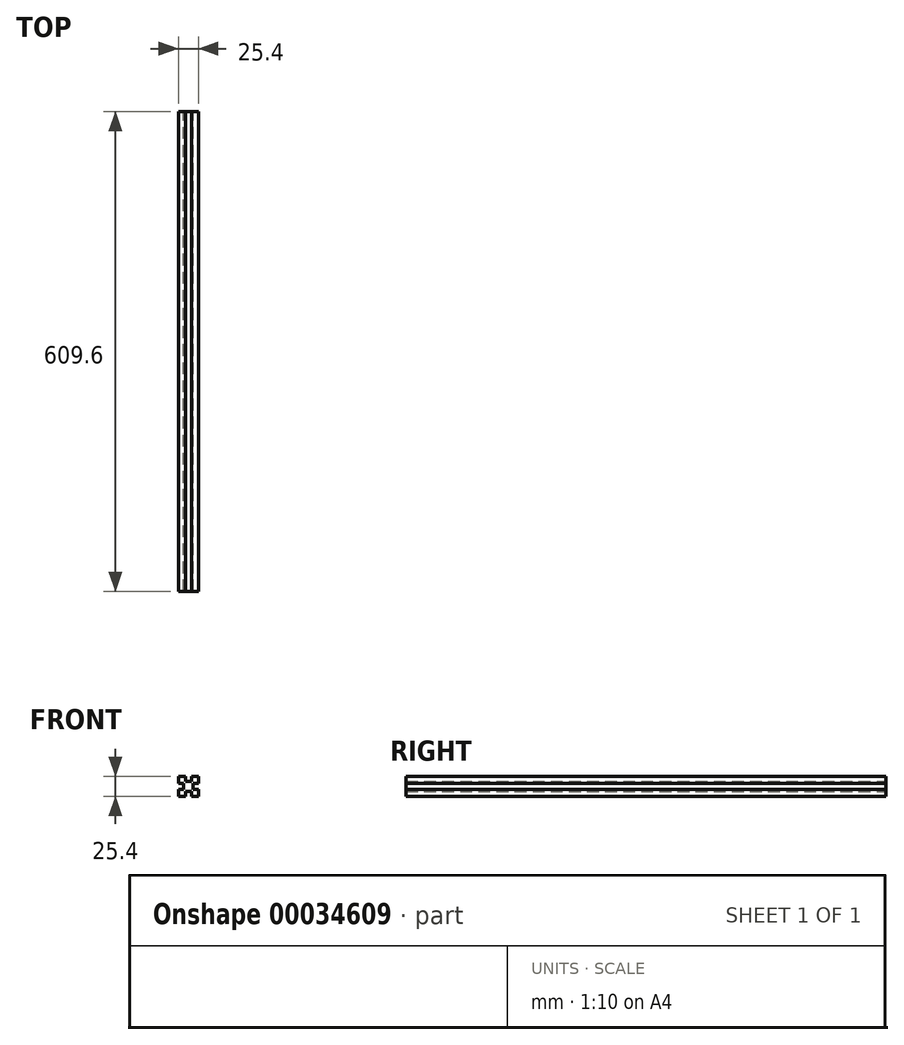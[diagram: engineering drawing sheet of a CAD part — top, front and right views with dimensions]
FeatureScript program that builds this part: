
annotation { "Feature Type Name" : "Feature", "Feature Type Description" : "" }
export const myFeature = defineFeature(function(context is Context, id is Id, definition is map)
    precondition{}
    {
        {
            var Q0;
            Q0=qCreatedBy(makeId("Front.planeOp"),FACE);
            var sketch = newSketch(context, id + "F0", { "sketchPlane" : qUnion([Q0])});
            skLineSegment(sketch, "E0.bottom", {"start": v(0, 0) * mm, "end": v(8.9, 0) * mm});
            skLineSegment(sketch, "E0.top", {"start": v(0, 25.4) * mm, "end": v(8.89, 25.4) * mm});
            skLineSegment(sketch, "E0.left", {"start": v(0, 0) * mm, "end": v(0, 8.9) * mm});
            skLineSegment(sketch, "E0.right", {"start": v(25.4, 0) * mm, "end": v(25.4, 8.89) * mm});
            skLineSegment(sketch, "E1.top", {"start": v(8.89, 19.05) * mm, "end": v(16.51, 19.05) * mm});
            skLineSegment(sketch, "E1.left", {"start": v(8.89, 25.4) * mm, "end": v(8.89, 19.05) * mm});
            skLineSegment(sketch, "E1.right", {"start": v(16.51, 25.4) * mm, "end": v(16.51, 19.05) * mm});
            skLineSegment(sketch, "E2.bottom", {"start": v(0, 16.5) * mm, "end": v(6.35, 16.5) * mm});
            skLineSegment(sketch, "E2.top", {"start": v(0, 8.9) * mm, "end": v(6.35, 8.9) * mm});
            skLineSegment(sketch, "E2.right", {"start": v(6.35, 16.5) * mm, "end": v(6.35, 8.9) * mm});
            skLineSegment(sketch, "E3.bottom", {"start": v(8.89, 6.35) * mm, "end": v(16.5, 6.35) * mm});
            skLineSegment(sketch, "E3.left", {"start": v(8.9, 6.35) * mm, "end": v(8.9, 0) * mm});
            skLineSegment(sketch, "E3.right", {"start": v(16.5, 6.35) * mm, "end": v(16.5, 0) * mm});
            skLineSegment(sketch, "E4.bottom", {"start": v(19.05, 16.5) * mm, "end": v(25.4, 16.5) * mm});
            skLineSegment(sketch, "E4.top", {"start": v(19.05, 8.89) * mm, "end": v(25.4, 8.89) * mm});
            skLineSegment(sketch, "E4.left", {"start": v(19.05, 16.5) * mm, "end": v(19.05, 8.89) * mm});
            skLineSegment(sketch, "E5.trimOffspring", {"start": v(0, 16.5) * mm, "end": v(0, 25.4) * mm});
            skLineSegment(sketch, "E6.trimOffspring", {"start": v(25.4, 16.5) * mm, "end": v(25.4, 25.4) * mm});
            skLineSegment(sketch, "E7.trimOffspring", {"start": v(16.5, 0) * mm, "end": v(25.4, 0) * mm});
            skLineSegment(sketch, "E8.trimOffspring", {"start": v(16.51, 25.4) * mm, "end": v(25.4, 25.4) * mm});
            skSolve(sketch);
        }
        {
            var Q0;
            Q0=qSketchRegion(id+"F0",true);
            extrude(context, id + "F1", {"entities" : qUnion([Q0]), "depth" : 609.6 * mm});
        }
    });
